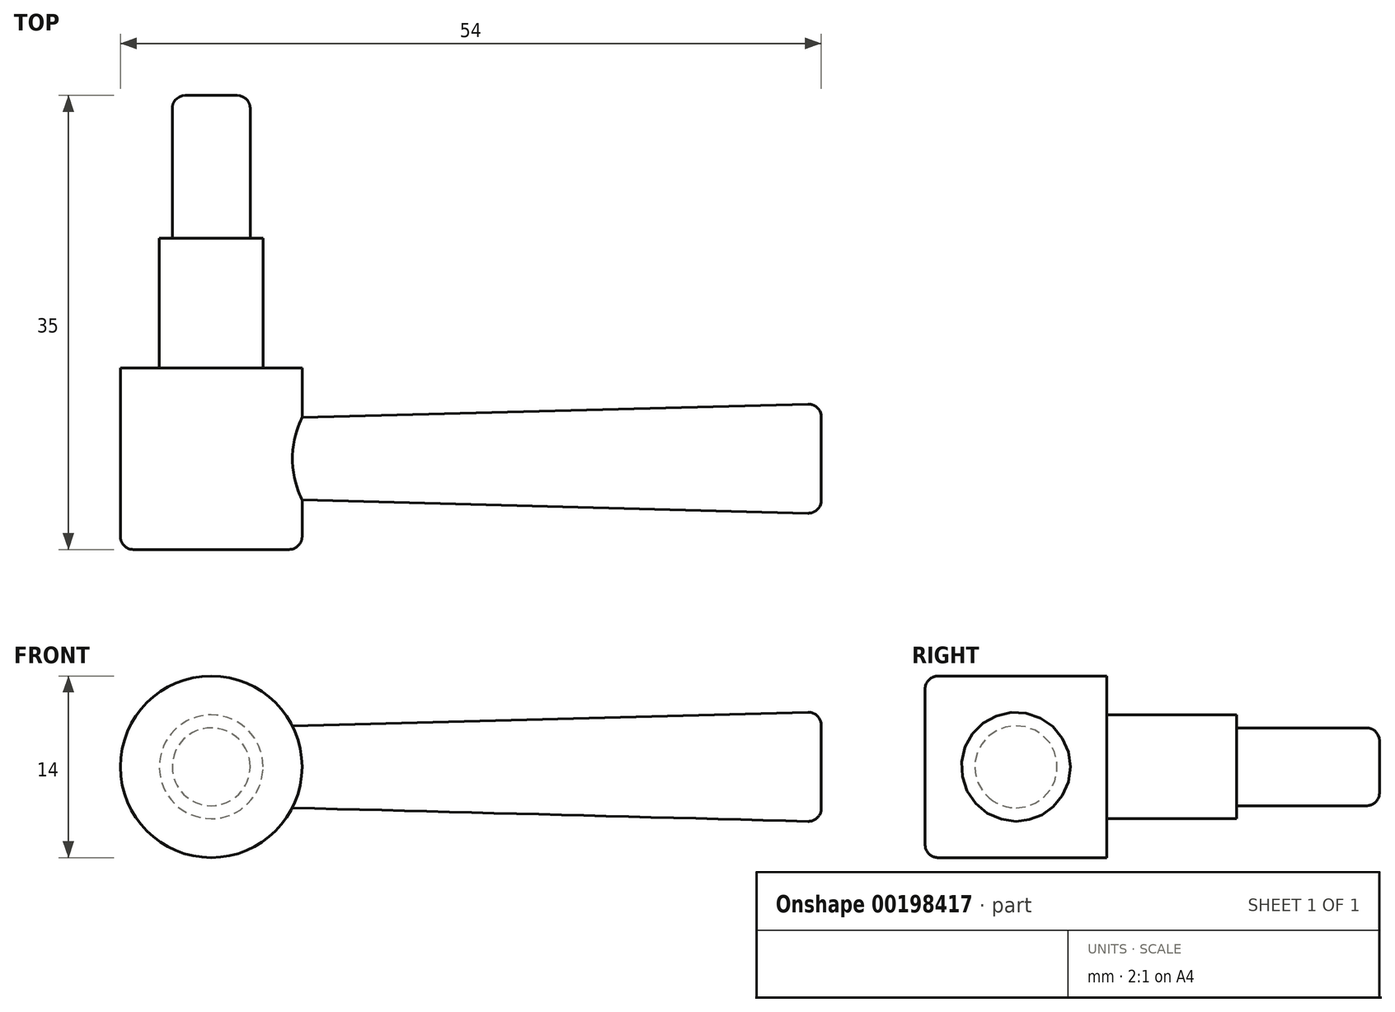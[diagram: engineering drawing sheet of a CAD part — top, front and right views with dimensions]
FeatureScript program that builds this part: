
annotation { "Feature Type Name" : "Feature", "Feature Type Description" : "" }
export const myFeature = defineFeature(function(context is Context, id is Id, definition is map)
    precondition{}
    {
        {
            var Q0;
            Q0=qCreatedBy(makeId("Front.planeOp"),FACE);
            var sketch = newSketch(context, id + "F0", { "sketchPlane" : qUnion([Q0])});
            skCircle(sketch, "E0", {"center": v(0, 0) * mm, "radius": 3 * mm});
            skCircle(sketch, "E1", {"center": v(0, 0) * mm, "radius": 4 * mm});
            skCircle(sketch, "E2", {"center": v(0, 0) * mm, "radius": 7 * mm});
            skSolve(sketch);
        }
        {
            var Q0;
            Q0 = qSketchRegion(id + "F0", true);
            extrude(context, id + "F1", {"entities" : qUnion([Q0]), "depth" : 24 * mm, "hasSecondDirection" : true, "secondDirectionOppositeDirection" : false, "secondDirectionDepth" : 10 * mm});
        }
        {
            var Q0;
            Q0=makeQuery(id+"F0.imprint","IMPRINT",FACE,{"disambiguationData":[TD([[makeQuery(id+"F0.imprint","IMPRINT",EDGE,{"derivedFrom":sQuery(id+"F0.wireOp",EDGE,"E0")}),1.0]])]});
            extrude(context, id + "F2", {"entities" : qUnion([Q0]), "depth" : 24 * mm, "hasSecondDirection" : true, "secondDirectionOppositeDirection" : true, "secondDirectionDepth" : 11 * mm});
        }
        {
            var Q0;
            Q0=makeQuery(id+"F0.imprint","IMPRINT",FACE,{"disambiguationData":[TD([[makeQuery(id+"F0.imprint","IMPRINT",EDGE,{"derivedFrom":sQuery(id+"F0.wireOp",EDGE,"E0")}),-1.0]])]});
            extrude(context, id + "F3", {"entities" : qUnion([Q0]), "depth" : 24 * mm});
        }
        {
            var Q0;
            Q0=qCreatedBy(makeId("Right.planeOp"),FACE);
            var sketch = newSketch(context, id + "F4", { "sketchPlane" : qUnion([Q0])});
            skCircle(sketch, "E3", {"center": v(-17, 0) * mm, "radius": 3 * mm});
            skSolve(sketch);
        }
        {
            var Q0;
            Q0 = qSketchRegion(id + "F4", true);
            extrude(context, id + "F5", {"entities" : qUnion([Q0]), "operationType" : NewBodyOperationType.ADD, "depth" : 47 * mm, "hasDraft" : true, "draftAngle" : 1.5 * degree});
        }
        {
            var Q0;
            Q0=makeQuery(id+"F1.opExtrude","CAP_EDGE",EDGE,{"disambiguationData":[OSD([sQuery(id+"F0.wireOp",EDGE,"E2")])],"isStart":false});
            var Q1;
            Q1=makeQuery(id+"F5.opExtrude","CAP_EDGE",EDGE,{"disambiguationData":[OSD([sQuery(id+"F4.wireOp",EDGE,"E3")])],"isStart":false});
            var Q2;
            Q2=makeQuery(id+"F2.opExtrude","CAP_EDGE",EDGE,{"disambiguationData":[OSD([sQuery(id+"F0.wireOp",EDGE,"E0")])],"isStart":true});
            fillet(context, id + "F6", {"entities" : qUnion([Q0, Q1, Q2]), "radius" : 1 * mm, "tangentPropagation" : true, "allowEdgeOverflow" : false});
        }
    });
